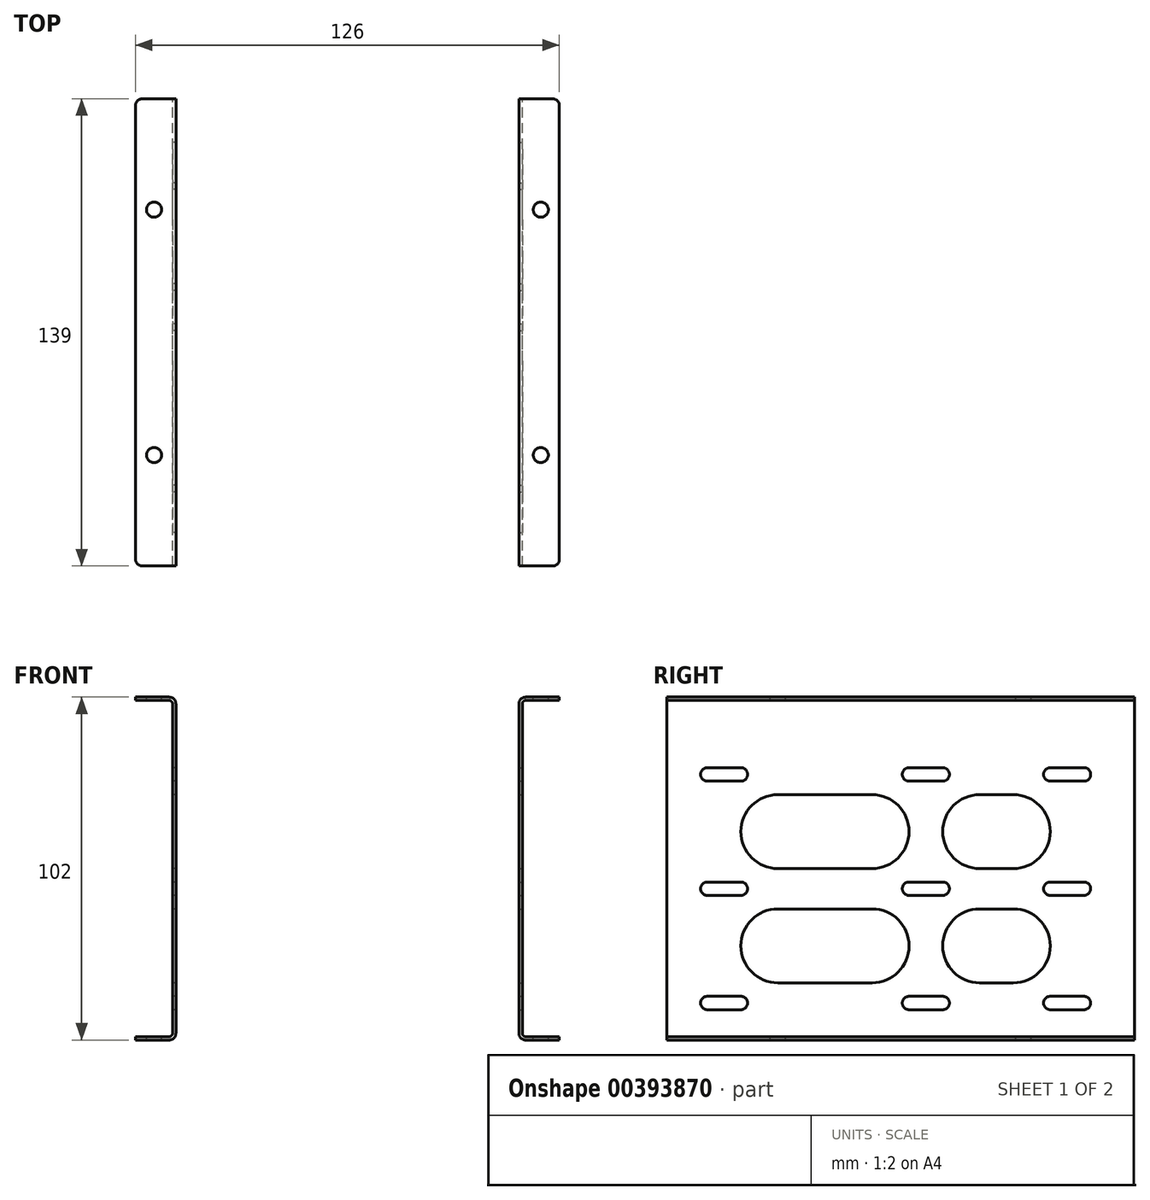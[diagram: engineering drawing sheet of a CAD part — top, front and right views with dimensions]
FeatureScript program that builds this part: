
annotation { "Feature Type Name" : "Feature", "Feature Type Description" : "" }
export const myFeature = defineFeature(function(context is Context, id is Id, definition is map)
    precondition{}
    {
        {
            var Q0;
            Q0=qCreatedBy(makeId("Front.planeOp"),FACE);
            var sketch = newSketch(context, id + "F0", { "sketchPlane" : qUnion([Q0])});
            skLineSegment(sketch, "E0", {"start": v(0, 0) * mm, "end": v(10, 0) * mm});
            skLineSegment(sketch, "E1", {"start": v(12, 2) * mm, "end": v(12, 100) * mm});
            skLineSegment(sketch, "E2", {"start": v(10, 102) * mm, "end": v(0, 102) * mm});
            skLineSegment(sketch, "E3.0", {"start": v(0, 1) * mm, "end": v(10, 1) * mm});
            skLineSegment(sketch, "E4.0", {"start": v(11, 2) * mm, "end": v(11, 100) * mm});
            skLineSegment(sketch, "E5.0", {"start": v(10, 101) * mm, "end": v(0, 101) * mm});
            skLineSegment(sketch, "E6", {"start": v(0, 101) * mm, "end": v(0, 102) * mm});
            skLineSegment(sketch, "E7", {"start": v(0, 0) * mm, "end": v(0, 1) * mm});
            skPoint(sketch, "E8.visualSharp", {"position": v(11, 1) * mm});
            skArc(sketch, "E8.filletArc", {"start": v(10, 1) * mm, "mid": v(10.7, 1.3) * mm, "end": v(11, 2) * mm});
            skPoint(sketch, "E9.visualSharp", {"position": v(12, 0) * mm});
            skArc(sketch, "E9.filletArc", {"start": v(10, 0) * mm, "mid": v(11.41, 0.59) * mm, "end": v(12, 2) * mm});
            skPoint(sketch, "E10.visualSharp", {"position": v(11, 101) * mm});
            skArc(sketch, "E10.filletArc", {"start": v(11, 100) * mm, "mid": v(10.7, 100.7) * mm, "end": v(10, 101) * mm});
            skPoint(sketch, "E11.visualSharp", {"position": v(12, 102) * mm});
            skArc(sketch, "E11.filletArc", {"start": v(12, 100) * mm, "mid": v(11.41, 101.41) * mm, "end": v(10, 102) * mm});
            skSolve(sketch);
        }
        {
            var Q0;
            Q0 = qSketchRegion(id + "F0", true);
            extrude(context, id + "F1", {"entities" : qUnion([Q0]), "depth" : 139 * mm});
        }
        {
            var Q0;
            Q0=makeQuery(id+"F1.opExtrude","SWEPT_FACE",FACE,{"disambiguationData":[OSD([sQuery(id+"F0.wireOp",EDGE,"E2")])]});
            var sketch = newSketch(context, id + "F2", { "sketchPlane" : qUnion([Q0])});
            skCircle(sketch, "E12", {"center": v(5.5, -33) * mm, "radius": 2.25 * mm});
            skCircle(sketch, "E13.0.1.0", {"center": v(5.5, -106) * mm, "radius": 2.25 * mm});
            skLineSegment(sketch, "E13.direction1", {"start": v(5.5, -33) * mm, "end": v(30.5, -33) * mm, "construction": true});
            skLineSegment(sketch, "E13.direction2", {"start": v(5.5, -33) * mm, "end": v(5.5, -106) * mm, "construction": true});
            skSolve(sketch);
        }
        {
            var Q0;
            Q0=sQuery(id+"F2.wireOp",VERTEX,"E13.0.1.0.center");
            var Q1;
            Q1=sQuery(id+"F2.wireOp",VERTEX,"E12.center");
            var Q2;
            Q2=makeQuery(id+"F1.opExtrude","SWEPT_BODY",BODY,{"disambiguationData":[OSD([sQuery(id+"F0.wireOp",EDGE,"E0"),sQuery(id+"F0.wireOp",EDGE,"E1"),sQuery(id+"F0.wireOp",EDGE,"E2"),sQuery(id+"F0.wireOp",EDGE,"E3.0"),sQuery(id+"F0.wireOp",EDGE,"E4.0"),sQuery(id+"F0.wireOp",EDGE,"E5.0"),sQuery(id+"F0.wireOp",EDGE,"E6"),sQuery(id+"F0.wireOp",EDGE,"E7"),sQuery(id+"F0.wireOp",EDGE,"E8.filletArc"),sQuery(id+"F0.wireOp",EDGE,"E9.filletArc"),sQuery(id+"F0.wireOp",EDGE,"E10.filletArc"),sQuery(id+"F0.wireOp",EDGE,"E11.filletArc")])]});
            hole(context, id + "F3", {"style" : HoleStyle.SIMPLE, "endStyle" : HoleEndStyle.THROUGH, "holeDiameter" : 4.5 * mm, "isTappedThrough" : true, "tappedDepth" : 12 * mm, "tapClearance" : 3, "locations" : qUnion([Q0, Q1]), "scope" : qUnion([Q2])});
        }
        {
            var Q0;
            Q0=makeQuery(id+"F1.opExtrude","SWEPT_FACE",FACE,{"disambiguationData":[OSD([sQuery(id+"F0.wireOp",EDGE,"E4.0")])]});
            var sketch = newSketch(context, id + "F4", { "sketchPlane" : qUnion([Q0])});
            skLineSegment(sketch, "E14", {"start": v(15, 13) * mm, "end": v(25, 13) * mm});
            skLineSegment(sketch, "E15", {"start": v(15, 9) * mm, "end": v(25, 9) * mm});
            skArc(sketch, "E16", {"start": v(25, 13) * mm, "mid": v(27, 11) * mm, "end": v(25, 9) * mm});
            skArc(sketch, "E17", {"start": v(15, 13) * mm, "mid": v(13, 11) * mm, "end": v(15, 9) * mm});
            skPoint(sketch, "E18", {"position": v(20, 11) * mm});
            skPoint(sketch, "E19.0.1.0", {"position": v(20, 45) * mm});
            skArc(sketch, "E19.0.1.1", {"start": v(15, 47) * mm, "mid": v(13, 45) * mm, "end": v(15, 43) * mm});
            skLineSegment(sketch, "E19.0.1.2", {"start": v(15, 47) * mm, "end": v(25, 47) * mm});
            skLineSegment(sketch, "E19.0.1.3", {"start": v(15, 43) * mm, "end": v(25, 43) * mm});
            skArc(sketch, "E19.0.1.4", {"start": v(25, 47) * mm, "mid": v(27, 45) * mm, "end": v(25, 43) * mm});
            skPoint(sketch, "E19.0.2.0", {"position": v(20, 79) * mm});
            skArc(sketch, "E19.0.2.1", {"start": v(15, 81) * mm, "mid": v(13, 79) * mm, "end": v(15, 77) * mm});
            skLineSegment(sketch, "E19.0.2.2", {"start": v(15, 81) * mm, "end": v(25, 81) * mm});
            skLineSegment(sketch, "E19.0.2.3", {"start": v(15, 77) * mm, "end": v(25, 77) * mm});
            skArc(sketch, "E19.0.2.4", {"start": v(25, 81) * mm, "mid": v(27, 79) * mm, "end": v(25, 77) * mm});
            skPoint(sketch, "E19.1.0.0", {"position": v(62, 11) * mm});
            skArc(sketch, "E19.1.0.1", {"start": v(57, 13) * mm, "mid": v(55, 11) * mm, "end": v(57, 9) * mm});
            skLineSegment(sketch, "E19.1.0.2", {"start": v(57, 13) * mm, "end": v(67, 13) * mm});
            skLineSegment(sketch, "E19.1.0.3", {"start": v(57, 9) * mm, "end": v(67, 9) * mm});
            skArc(sketch, "E19.1.0.4", {"start": v(67, 13) * mm, "mid": v(69, 11) * mm, "end": v(67, 9) * mm});
            skPoint(sketch, "E19.1.1.0", {"position": v(62, 45) * mm});
            skArc(sketch, "E19.1.1.1", {"start": v(57, 47) * mm, "mid": v(55, 45) * mm, "end": v(57, 43) * mm});
            skLineSegment(sketch, "E19.1.1.2", {"start": v(57, 47) * mm, "end": v(67, 47) * mm});
            skLineSegment(sketch, "E19.1.1.3", {"start": v(57, 43) * mm, "end": v(67, 43) * mm});
            skArc(sketch, "E19.1.1.4", {"start": v(67, 47) * mm, "mid": v(69, 45) * mm, "end": v(67, 43) * mm});
            skPoint(sketch, "E19.1.2.0", {"position": v(62, 79) * mm});
            skArc(sketch, "E19.1.2.1", {"start": v(57, 81) * mm, "mid": v(55, 79) * mm, "end": v(57, 77) * mm});
            skLineSegment(sketch, "E19.1.2.2", {"start": v(57, 81) * mm, "end": v(67, 81) * mm});
            skLineSegment(sketch, "E19.1.2.3", {"start": v(57, 77) * mm, "end": v(67, 77) * mm});
            skArc(sketch, "E19.1.2.4", {"start": v(67, 81) * mm, "mid": v(69, 79) * mm, "end": v(67, 77) * mm});
            skLineSegment(sketch, "E19.direction1", {"start": v(20, 11) * mm, "end": v(62, 11) * mm, "construction": true});
            skLineSegment(sketch, "E19.direction2", {"start": v(20, 11) * mm, "end": v(20, 45) * mm, "construction": true});
            skPoint(sketch, "E20.1.0.0", {"position": v(122, 11) * mm});
            skLineSegment(sketch, "E20.1.0.1", {"start": v(117, 13) * mm, "end": v(127, 13) * mm});
            skArc(sketch, "E20.1.0.2", {"start": v(117, 13) * mm, "mid": v(115, 11) * mm, "end": v(117, 9) * mm});
            skLineSegment(sketch, "E20.1.0.3", {"start": v(117, 9) * mm, "end": v(127, 9) * mm});
            skArc(sketch, "E20.1.0.4", {"start": v(127, 13) * mm, "mid": v(129, 11) * mm, "end": v(127, 9) * mm});
            skPoint(sketch, "E20.1.1.0", {"position": v(122, 45) * mm});
            skLineSegment(sketch, "E20.1.1.1", {"start": v(117, 47) * mm, "end": v(127, 47) * mm});
            skArc(sketch, "E20.1.1.2", {"start": v(117, 47) * mm, "mid": v(115, 45) * mm, "end": v(117, 43) * mm});
            skLineSegment(sketch, "E20.1.1.3", {"start": v(117, 43) * mm, "end": v(127, 43) * mm});
            skArc(sketch, "E20.1.1.4", {"start": v(127, 47) * mm, "mid": v(129, 45) * mm, "end": v(127, 43) * mm});
            skPoint(sketch, "E20.1.2.0", {"position": v(122, 79) * mm});
            skLineSegment(sketch, "E20.1.2.1", {"start": v(117, 81) * mm, "end": v(127, 81) * mm});
            skArc(sketch, "E20.1.2.2", {"start": v(117, 81) * mm, "mid": v(115, 79) * mm, "end": v(117, 77) * mm});
            skLineSegment(sketch, "E20.1.2.3", {"start": v(117, 77) * mm, "end": v(127, 77) * mm});
            skArc(sketch, "E20.1.2.4", {"start": v(127, 81) * mm, "mid": v(129, 79) * mm, "end": v(127, 77) * mm});
            skLineSegment(sketch, "E20.direction1", {"start": v(62, 11) * mm, "end": v(122, 11) * mm, "construction": true});
            skLineSegment(sketch, "E20.direction2", {"start": v(62, 11) * mm, "end": v(62, 45) * mm, "construction": true});
            skSolve(sketch);
        }
        {
            var Q0;
            Q0 = qSketchRegion(id + "F4", true);
            extrude(context, id + "F5", {"entities" : qUnion([Q0]), "operationType" : NewBodyOperationType.REMOVE, "oppositeDirection" : true, "depth" : 25 * mm});
        }
        {
            var Q0;
            Q0=makeQuery(id+"F1.opExtrude","CAP_EDGE",EDGE,{"disambiguationData":[OSD([sQuery(id+"F0.wireOp",EDGE,"E6")])],"isStart":false});
            fillet(context, id + "F6", {"entities" : qUnion([Q0]), "radius" : 2 * mm, "tangentPropagation" : true, "allowEdgeOverflow" : false});
        }
        {
            var Q0;
            Q0=makeQuery(id+"F1.opExtrude","CAP_EDGE",EDGE,{"disambiguationData":[OSD([sQuery(id+"F0.wireOp",EDGE,"E7")])],"isStart":false});
            fillet(context, id + "F7", {"entities" : qUnion([Q0]), "radius" : 2 * mm, "allowEdgeOverflow" : false});
        }
        {
            var Q0;
            Q0=makeQuery(id+"F1.opExtrude","CAP_EDGE",EDGE,{"disambiguationData":[OSD([sQuery(id+"F0.wireOp",EDGE,"E7")])],"isStart":true});
            fillet(context, id + "F8", {"entities" : qUnion([Q0]), "radius" : 2 * mm, "tangentPropagation" : true, "allowEdgeOverflow" : false});
        }
        {
            var Q0;
            Q0=makeQuery(id+"F1.opExtrude","CAP_EDGE",EDGE,{"disambiguationData":[OSD([sQuery(id+"F0.wireOp",EDGE,"E6")])],"isStart":true});
            fillet(context, id + "F9", {"entities" : qUnion([Q0]), "radius" : 2 * mm, "tangentPropagation" : true, "allowEdgeOverflow" : false});
        }
        {
            var Q0;
            Q0=makeQuery(id+"F1.opExtrude","SWEPT_FACE",FACE,{"disambiguationData":[OSD([sQuery(id+"F0.wireOp",EDGE,"E4.0")])]});
            var sketch = newSketch(context, id + "F10", { "sketchPlane" : qUnion([Q0])});
            skLineSegment(sketch, "E21", {"start": v(36, 39) * mm, "end": v(46, 39) * mm});
            skLineSegment(sketch, "E22", {"start": v(36, 17) * mm, "end": v(46, 17) * mm});
            skArc(sketch, "E23", {"start": v(36, 39) * mm, "mid": v(25, 28) * mm, "end": v(36, 17) * mm});
            skArc(sketch, "E24", {"start": v(46, 39) * mm, "mid": v(57, 28) * mm, "end": v(46, 17) * mm});
            skPoint(sketch, "E25", {"position": v(41, 28) * mm});
            skPoint(sketch, "E26.0.1.0", {"position": v(41, 62) * mm});
            skLineSegment(sketch, "E26.0.1.1", {"start": v(36, 73) * mm, "end": v(46, 73) * mm});
            skArc(sketch, "E26.0.1.2", {"start": v(36, 73) * mm, "mid": v(25, 62) * mm, "end": v(36, 51) * mm});
            skLineSegment(sketch, "E26.0.1.3", {"start": v(36, 51) * mm, "end": v(46, 51) * mm});
            skArc(sketch, "E26.0.1.4", {"start": v(46, 73) * mm, "mid": v(57, 62) * mm, "end": v(46, 51) * mm});
            skLineSegment(sketch, "E26.direction1", {"start": v(36, 17) * mm, "end": v(61, 17) * mm, "construction": true});
            skLineSegment(sketch, "E26.direction2", {"start": v(36, 17) * mm, "end": v(36, 51) * mm, "construction": true});
            skLineSegment(sketch, "E27", {"start": v(78, 39) * mm, "end": v(106, 39) * mm});
            skLineSegment(sketch, "E28", {"start": v(78, 17) * mm, "end": v(106, 17) * mm});
            skArc(sketch, "E29", {"start": v(78, 39) * mm, "mid": v(67, 28) * mm, "end": v(78, 17) * mm});
            skArc(sketch, "E30", {"start": v(106, 39) * mm, "mid": v(117, 28) * mm, "end": v(106, 17) * mm});
            skPoint(sketch, "E31", {"position": v(92, 28) * mm});
            skPoint(sketch, "E32.0.1.0", {"position": v(92, 62) * mm});
            skLineSegment(sketch, "E32.0.1.1", {"start": v(78, 51) * mm, "end": v(106, 51) * mm});
            skLineSegment(sketch, "E32.0.1.2", {"start": v(78, 73) * mm, "end": v(106, 73) * mm});
            skArc(sketch, "E32.0.1.3", {"start": v(78, 73) * mm, "mid": v(67, 62) * mm, "end": v(78, 51) * mm});
            skArc(sketch, "E32.0.1.4", {"start": v(106, 73) * mm, "mid": v(117, 62) * mm, "end": v(106, 51) * mm});
            skLineSegment(sketch, "E32.direction1", {"start": v(78, 17) * mm, "end": v(103, 17) * mm, "construction": true});
            skLineSegment(sketch, "E32.direction2", {"start": v(78, 17) * mm, "end": v(78, 51) * mm, "construction": true});
            skSolve(sketch);
        }
        {
            var Q0;
            Q0 = qSketchRegion(id + "F10", true);
            extrude(context, id + "F11", {"entities" : qUnion([Q0]), "operationType" : NewBodyOperationType.REMOVE, "oppositeDirection" : true, "depth" : 25 * mm});
        }
        {
            var Q0;
            Q0=qCreatedBy(makeId("Right.planeOp"),FACE);
            cPlane(context, id + "F12", {"entities" : qUnion([Q0]), "cplaneType" : CPlaneType.OFFSET, "offset" : 63 * mm, "width" : 150 * mm, "height" : 150 * mm});
        }
        {
            var Q0;
            Q0=makeQuery(id+"F1.opExtrude","SWEPT_BODY",BODY,{"disambiguationData":[OSD([sQuery(id+"F0.wireOp",EDGE,"E0"),sQuery(id+"F0.wireOp",EDGE,"E1"),sQuery(id+"F0.wireOp",EDGE,"E2"),sQuery(id+"F0.wireOp",EDGE,"E3.0"),sQuery(id+"F0.wireOp",EDGE,"E4.0"),sQuery(id+"F0.wireOp",EDGE,"E5.0"),sQuery(id+"F0.wireOp",EDGE,"E6"),sQuery(id+"F0.wireOp",EDGE,"E7"),sQuery(id+"F0.wireOp",EDGE,"E8.filletArc"),sQuery(id+"F0.wireOp",EDGE,"E9.filletArc"),sQuery(id+"F0.wireOp",EDGE,"E10.filletArc"),sQuery(id+"F0.wireOp",EDGE,"E11.filletArc")])]});
            var Q1;
            Q1=qCreatedBy(id+"F12.planeOp",FACE);
            mirror(context, id + "F13", {"entities" : qUnion([Q0]), "mirrorPlane" : qUnion([Q1])});
        }
    });
